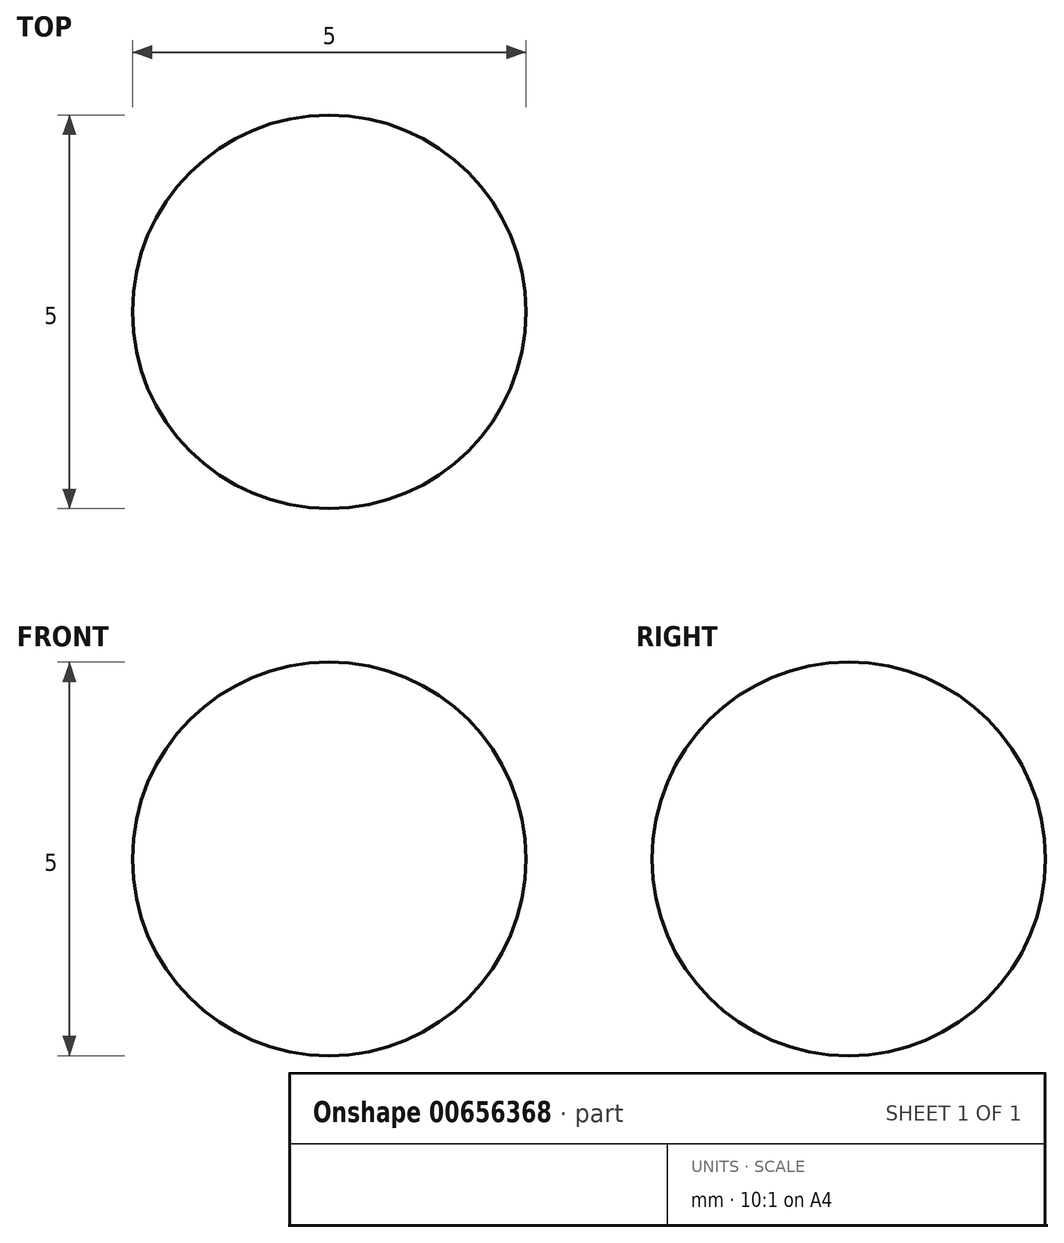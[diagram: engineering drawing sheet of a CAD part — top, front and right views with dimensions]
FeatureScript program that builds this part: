
annotation { "Feature Type Name" : "Feature", "Feature Type Description" : "" }
export const myFeature = defineFeature(function(context is Context, id is Id, definition is map)
    precondition{}
    {
        {
            var Q0;
            Q0=qCreatedBy(makeId("Front.planeOp"),FACE);
            var sketch = newSketch(context, id + "F0", { "sketchPlane" : qUnion([Q0])});
            skArc(sketch, "E0", {"start": v(0, 2.5) * mm, "mid": v(-2.5, 0) * mm, "end": v(0, -2.5) * mm});
            skLineSegment(sketch, "E1", {"start": v(0, 2.5) * mm, "end": v(0, -2.5) * mm});
            skLineSegment(sketch, "E2", {"start": v(0, 5.86) * mm, "end": v(0, -4.42) * mm, "construction": true});
            skSolve(sketch);
        }
        {
            var Q0;
            Q0 = qSketchRegion(id + "F0", true);
            var Q1;
            Q1=sQuery(id+"F0.wireOp",EDGE,"E2");
            revolve(context, id + "F1", {"entities" : qUnion([Q0]), "axis" : qUnion([Q1]), "revolveType" : RevolveType.FULL});
        }
    });
